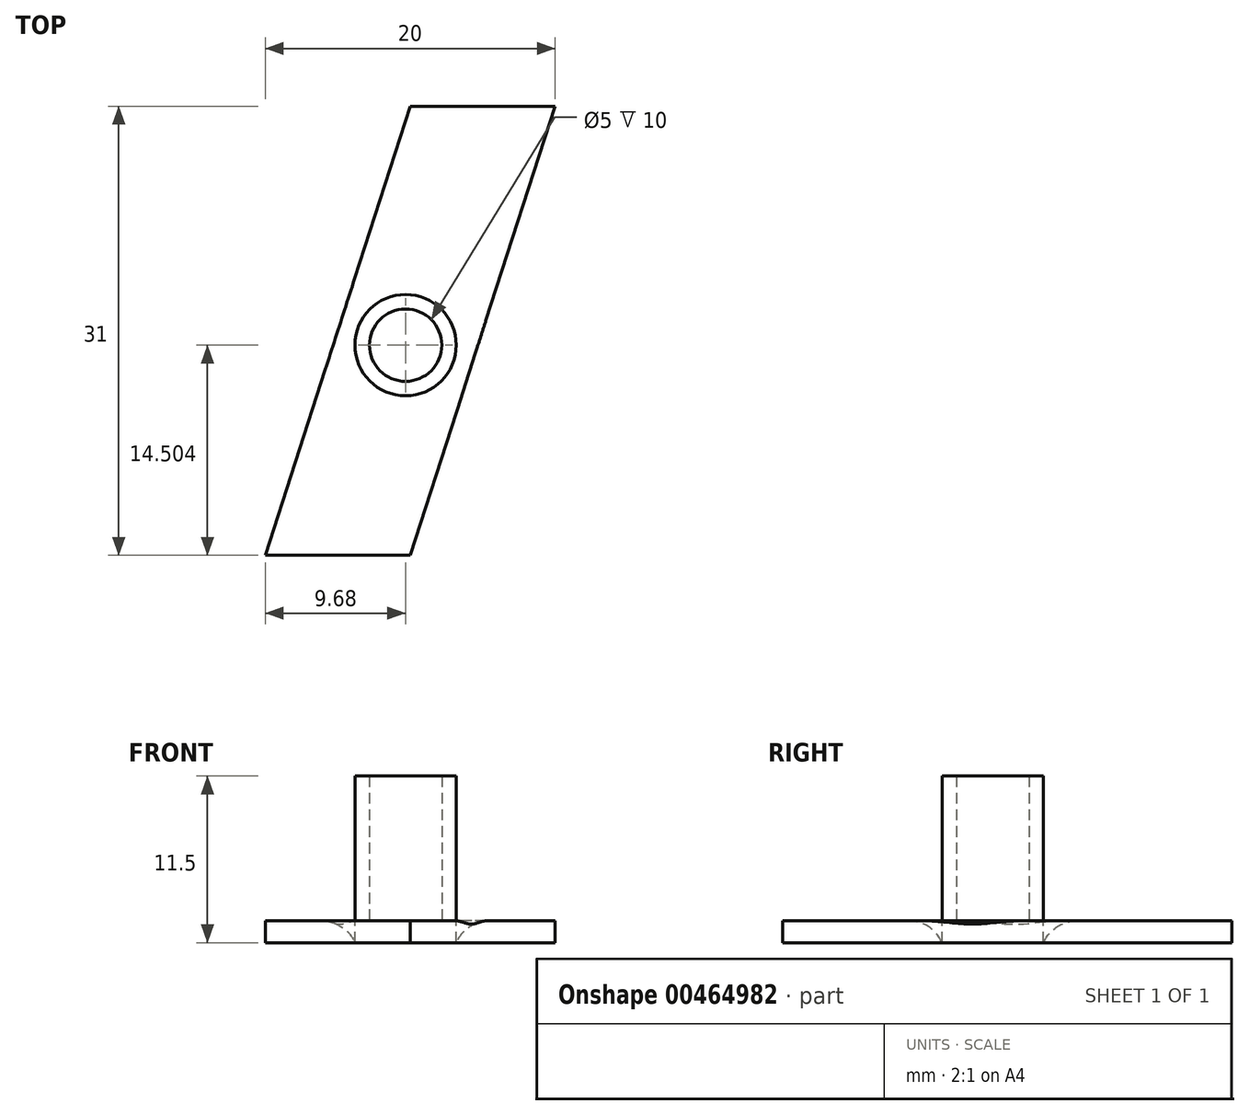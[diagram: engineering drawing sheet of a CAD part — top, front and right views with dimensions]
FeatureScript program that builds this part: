
annotation { "Feature Type Name" : "Feature", "Feature Type Description" : "" }
export const myFeature = defineFeature(function(context is Context, id is Id, definition is map)
    precondition{}
    {
        {
            var Q0;
            Q0=qCreatedBy(makeId("Top.planeOp"),FACE);
            var sketch = newSketch(context, id + "F0", { "sketchPlane" : qUnion([Q0])});
            skLineSegment(sketch, "E0", {"start": v(-24.03, -14.3) * mm, "end": v(-14.03, -14.3) * mm});
            skLineSegment(sketch, "E1", {"start": v(-14.03, -14.3) * mm, "end": v(-4.03, -14.3) * mm, "construction": true});
            skLineSegment(sketch, "E2", {"start": v(-4.03, -14.3) * mm, "end": v(-4.03, 16.7) * mm, "construction": true});
            skLineSegment(sketch, "E3", {"start": v(-4.03, 16.7) * mm, "end": v(-14.03, 16.7) * mm});
            skLineSegment(sketch, "E4", {"start": v(-14.03, 16.7) * mm, "end": v(-24.03, 16.7) * mm, "construction": true});
            skLineSegment(sketch, "E5", {"start": v(-24.03, 16.7) * mm, "end": v(-24.03, -14.3) * mm, "construction": true});
            skLineSegment(sketch, "E6", {"start": v(-14.03, -14.3) * mm, "end": v(-4.03, 16.7) * mm});
            skLineSegment(sketch, "E7", {"start": v(-24.03, -14.3) * mm, "end": v(-14.03, 16.7) * mm});
            skCircle(sketch, "E8", {"center": v(-14.35, 0.2) * mm, "radius": 2.5 * mm});
            skCircle(sketch, "E9.0", {"center": v(-14.35, 0.2) * mm, "radius": 3.5 * mm});
            skSolve(sketch);
        }
        {
            var Q0;
            Q0=makeQuery(id+"F0.imprint","IMPRINT",FACE,{"disambiguationData":[TD([[makeQuery(id+"F0.imprint","IMPRINT",EDGE,{"derivedFrom":sQuery(id+"F0.wireOp",EDGE,"E8")}),-1.0]])]});
            var Q1;
            Q1=sQuery(id+"F0.wireOp",EDGE,"E9.0");
            var Q2;
            Q2=sQuery(id+"F0.wireOp",EDGE,"E8");
            extrude(context, id + "F1", {"entities" : qUnion([Q0]), "surfaceEntities" : qUnion([Q1, Q2]), "depth" : 10 * mm});
        }
        {
            var Q0;
            Q0=makeQuery(id+"F0.imprint","IMPRINT",FACE,{"disambiguationData":[TD([[makeQuery(id+"F0.imprint","IMPRINT",EDGE,{"derivedFrom":sQuery(id+"F0.wireOp",EDGE,"E0")}),1.0]])]});
            extrude(context, id + "F2", {"entities" : qUnion([Q0]), "depth" : -1.5 * mm});
        }
        {
            var Q0;
            Q0=makeQuery(id+"F0.imprint","IMPRINT",FACE,{"disambiguationData":[TD([[makeQuery(id+"F0.imprint","IMPRINT",EDGE,{"derivedFrom":sQuery(id+"F0.wireOp",EDGE,"E8")}),-1.0]])]});
            var Q1;
            Q1=makeQuery(id+"F0.imprint","IMPRINT",FACE,{"disambiguationData":[TD([[makeQuery(id+"F0.imprint","IMPRINT",EDGE,{"derivedFrom":sQuery(id+"F0.wireOp",EDGE,"E8")}),1.0]])]});
            var Q2;
            Q2=sQuery(id+"F0.wireOp",EDGE,"E9.0");
            extrude(context, id + "F3", {"entities" : qUnion([Q0, Q1]), "surfaceEntities" : qUnion([Q2]), "depth" : -1.5 * mm});
        }
        {
            var Q0;
            Q0=makeQuery(id+"F2.opExtrude","CAP_EDGE",EDGE,{"disambiguationData":[OSD([sQuery(id+"F0.wireOp",EDGE,"E9.0")])],"isStart":true});
            fillet(context, id + "F4", {"entities" : qUnion([Q0]), "tangentPropagation" : true, "radius" : 2.5 * mm, "defaultsChanged" : true, "vertexSettings" : [], "allowEdgeOverflow" : false});
        }
    });
